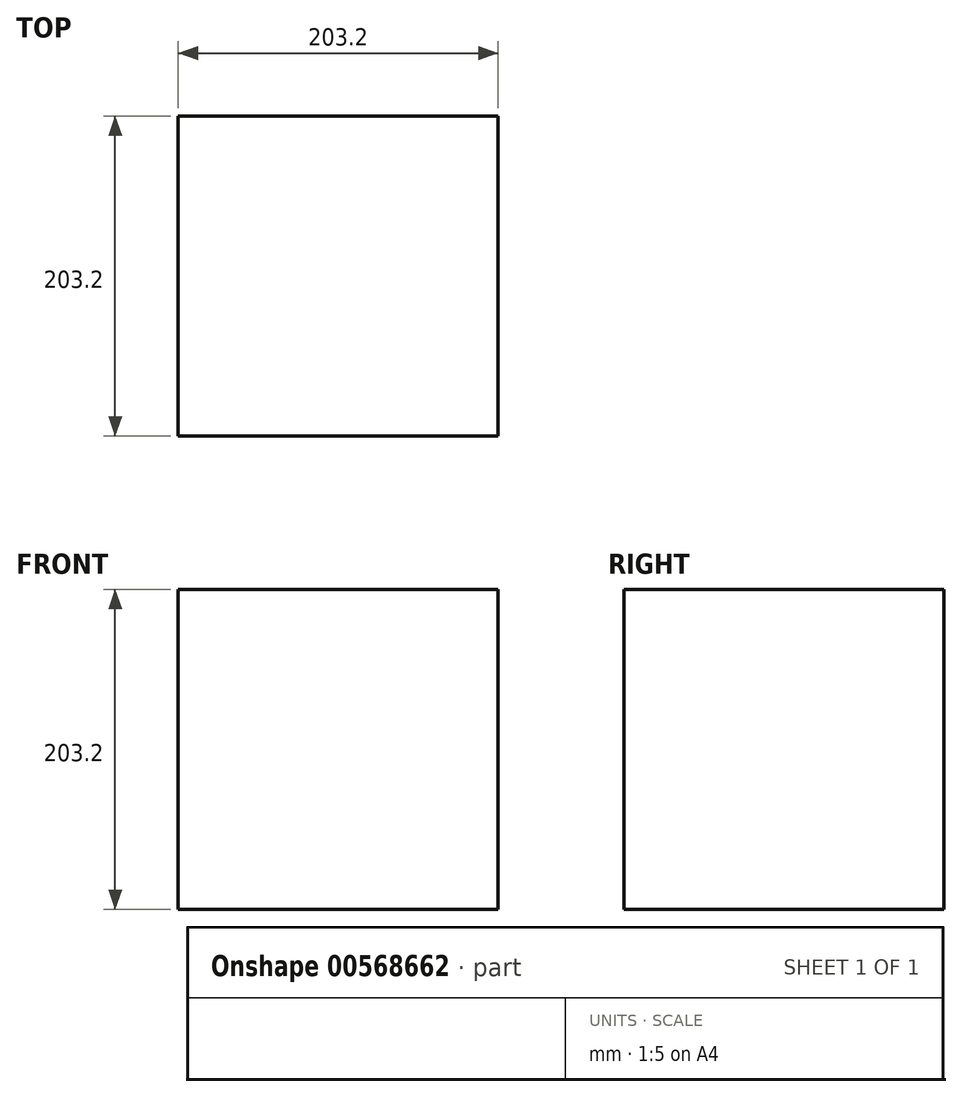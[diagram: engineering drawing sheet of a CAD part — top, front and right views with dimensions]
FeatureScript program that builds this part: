
annotation { "Feature Type Name" : "Feature", "Feature Type Description" : "" }
export const myFeature = defineFeature(function(context is Context, id is Id, definition is map)
    precondition{}
    {
        {
            var Q0;
            Q0=qCreatedBy(makeId("Front.planeOp"),FACE);
            var sketch = newSketch(context, id + "F0", { "sketchPlane" : qUnion([Q0])});
            skLineSegment(sketch, "E0.bottom", {"start": v(0, 0) * mm, "end": v(203.2, 0) * mm});
            skLineSegment(sketch, "E0.top", {"start": v(0, 203.2) * mm, "end": v(203.2, 203.2) * mm});
            skLineSegment(sketch, "E0.left", {"start": v(0, 0) * mm, "end": v(0, 203.2) * mm});
            skLineSegment(sketch, "E0.right", {"start": v(203.2, 0) * mm, "end": v(203.2, 203.2) * mm});
            skSolve(sketch);
        }
        {
            var Q0;
            Q0=makeQuery(id+"F0.imprint","IMPRINT",FACE,{"disambiguationData":[TD([[makeQuery(id+"F0.imprint","IMPRINT",EDGE,{"derivedFrom":sQuery(id+"F0.wireOp",EDGE,"E0.bottom")}),1.0]])]});
            extrude(context, id + "F1", {"entities" : qUnion([Q0]), "depth" : 203.2 * mm, "offsetDistance" : 25.4 * mm});
        }
        {
            var Q0;
            Q0=makeQuery(id+"F1.opExtrude","SWEPT_FACE",FACE,{"disambiguationData":[OSD([sQuery(id+"F0.wireOp",EDGE,"E0.left")])]});
            var sketch = newSketch(context, id + "F2", { "sketchPlane" : qUnion([Q0])});
            skCircle(sketch, "E1", {"center": v(102.34, 103.04) * mm, "radius": 25.4 * mm});
            skSolve(sketch);
        }
        {
            var Q0;
            Q0=makeQuery(id+"F2.imprint","IMPRINT",FACE,{"disambiguationData":[TD([[makeQuery(id+"F2.imprint","IMPRINT",EDGE,{"derivedFrom":sQuery(id+"F2.wireOp",EDGE,"E1")}),1.0]])]});
            extrude(context, id + "F3", {"entities" : qUnion([Q0]), "operationType" : NewBodyOperationType.REMOVE, "depth" : 203.2 * mm, "offsetDistance" : 25.4 * mm});
        }
    });
